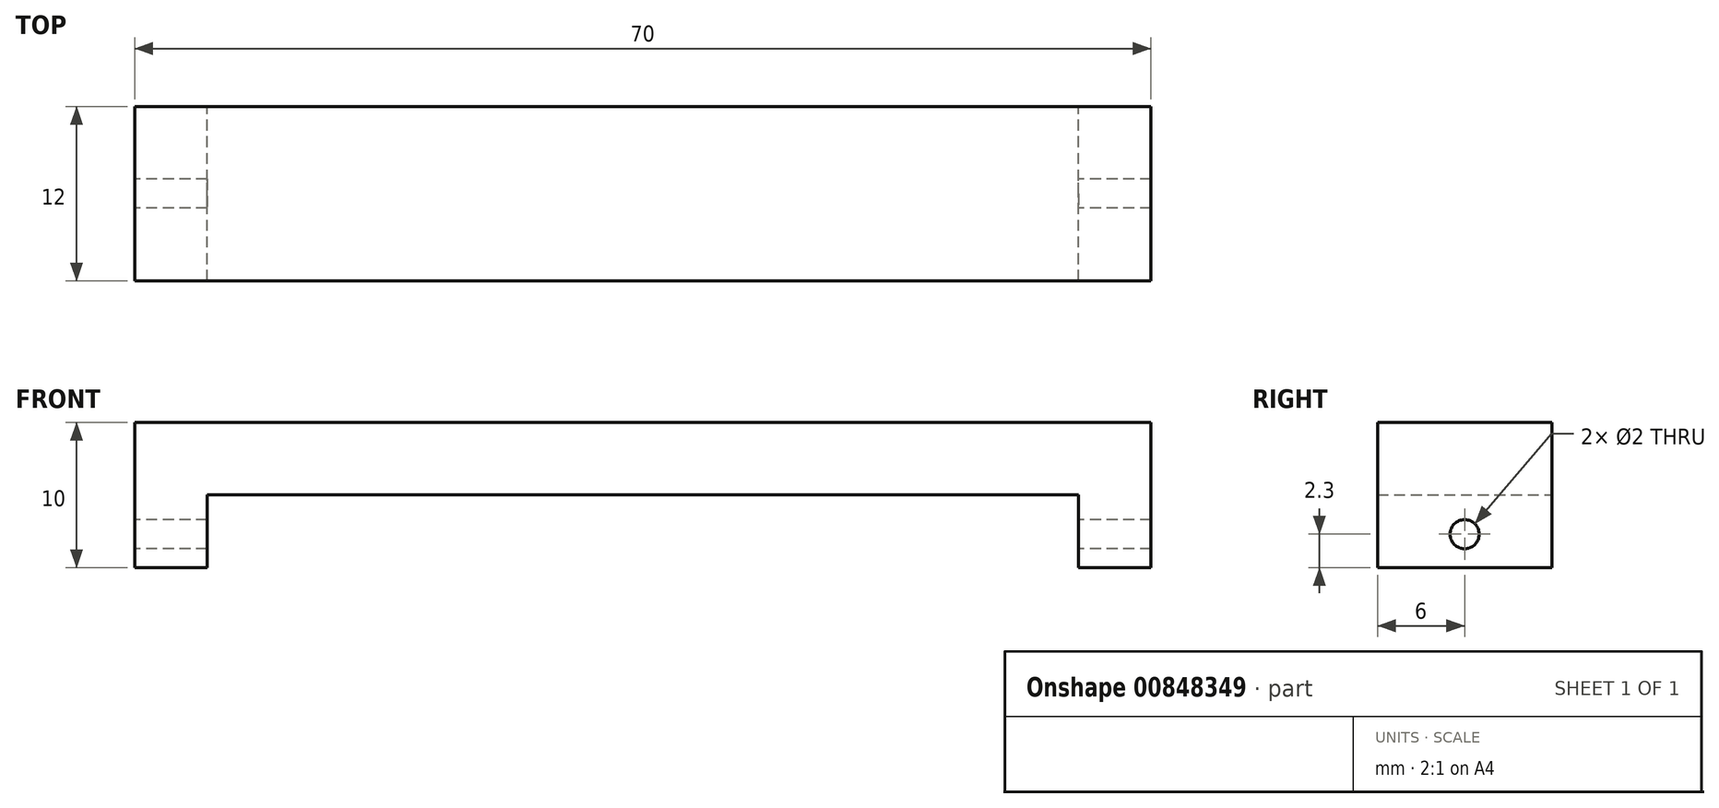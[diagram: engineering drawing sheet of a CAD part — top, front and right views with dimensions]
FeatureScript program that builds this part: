
annotation { "Feature Type Name" : "Feature", "Feature Type Description" : "" }
export const myFeature = defineFeature(function(context is Context, id is Id, definition is map)
    precondition{}
    {
        {
            var Q0;
            Q0=qCreatedBy(makeId("Front.planeOp"),FACE);
            var sketch = newSketch(context, id + "F0", { "sketchPlane" : qUnion([Q0])});
            skLineSegment(sketch, "E0", {"start": v(-35, -5) * mm, "end": v(-30, -5) * mm});
            skLineSegment(sketch, "E1", {"start": v(-30, -5) * mm, "end": v(-30, 0) * mm});
            skLineSegment(sketch, "E2", {"start": v(-30, 0) * mm, "end": v(30, 0) * mm});
            skLineSegment(sketch, "E3", {"start": v(30, 0) * mm, "end": v(30, -5) * mm});
            skLineSegment(sketch, "E4", {"start": v(30, -5) * mm, "end": v(35, -5) * mm});
            skLineSegment(sketch, "E5", {"start": v(35, -5) * mm, "end": v(35, 5) * mm});
            skLineSegment(sketch, "E6", {"start": v(35, 5) * mm, "end": v(-35, 5) * mm});
            skLineSegment(sketch, "E7", {"start": v(-35, 5) * mm, "end": v(-35, -5) * mm});
            skSolve(sketch);
        }
        {
            var Q0;
            Q0=makeQuery(id+"F0.imprint","IMPRINT",FACE,{"disambiguationData":[TD([[makeQuery(id+"F0.imprint","IMPRINT",EDGE,{"derivedFrom":sQuery(id+"F0.wireOp",EDGE,"E0")}),1.0]])]});
            extrude(context, id + "F1", {"entities" : qUnion([Q0]), "depth" : 12 * mm, "offsetDistance" : 25 * mm});
        }
        {
            var Q0;
            Q0=makeQuery(id+"F1.opExtrude","SWEPT_FACE",FACE,{"disambiguationData":[OSD([sQuery(id+"F0.wireOp",EDGE,"E7")])]});
            var sketch = newSketch(context, id + "F2", { "sketchPlane" : qUnion([Q0])});
            skCircle(sketch, "E8", {"center": v(6, -2.7) * mm, "radius": 1 * mm});
            skSolve(sketch);
        }
        {
            var Q0;
            Q0=makeQuery(id+"F2.imprint","IMPRINT",FACE,{"disambiguationData":[TD([[makeQuery(id+"F2.imprint","IMPRINT",EDGE,{"derivedFrom":sQuery(id+"F2.wireOp",EDGE,"E8")}),1.0]])]});
            extrude(context, id + "F3", {"entities" : qUnion([Q0]), "operationType" : NewBodyOperationType.REMOVE, "oppositeDirection" : true, "depth" : 70 * mm, "offsetDistance" : 25 * mm});
        }
    });
